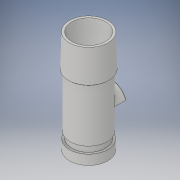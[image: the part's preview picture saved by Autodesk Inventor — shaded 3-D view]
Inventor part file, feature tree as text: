
AUTODESK INVENTOR PART (.ipt)
format: ipt  version: 2019.2 (Build 232265000, 265)  size: 415,232 bytes
history: native  units: mm
features: extrude x7, sketch x7, chamfer x2, other x1, fillet x1, plane x1, draft x1
ambient origin geometry x8: Origin, YZ Plane, XZ Plane, XY Plane, X Axis, Y Axis, Z Axis, Center Point
bodies: Solid1 (feature_tree)
feature tree (20):
  other  "CrossSection1"
  extrude  "Extrusion1"  Depth=35.0mm
  extrude  "Extrusion2"  Depth=9.0mm
  extrude  "Extrusion3"  Depth=50.0mm TaperAngle=0.0deg
  fillet  "Fillet1"  Radius=1.0mm
  plane  "Work Plane1"
  extrude  "Extrusion4"  Depth=10.0mm
  chamfer  "Chamfer1"  Distance=2.0mm
  extrude  "Extrusion5"  Depth=30.0mm
  extrude  "Extrusion6"  Depth=30.0mm
  chamfer  "Chamfer3"  Distance=10.0mm
  extrude  "Extrusion7"  Depth=30.0mm TaperAngle=0.0deg
  draft  "FaceDraft4"
  sketch  "Sketch1"  dims[d0=29.5mm d1=35.0mm]
  sketch  "Sketch2"  dims[d2=9.0mm d3=0.0mm d4=31.0mm]
  sketch  "Sketch3"  dims[d5=5.0mm d6=0.0mm d7=50.0mm d8=0.0mm d9=1.0mm]
  sketch  "Sketch4"  dims[d10=37.0mm d16=10.0mm]
  sketch  "Sketch5"  dims[d17=12.5mm]
  sketch  "Sketch6"  dims[d18=12.5mm]
  sketch  "Sketch9"  dims[d19=5.0mm d20=2.0mm d21=2.0mm d22=44.048322mm d23=10.0mm d24=0.0mm d25=4.0mm d26=0.0mm d27=1.5mm d28=2.0mm d29=45.0deg d30=1.5mm d31=0.0mm d32=37.0mm d33=30.0mm d34=0.0mm d38=0.5mm d39=2.0mm d40=45.0deg d44=0.5mm d45=2.0mm d46=-2.25mm d47=20.0mm d51=0.0mm d52=0.0mm d56=0.261799mm]
